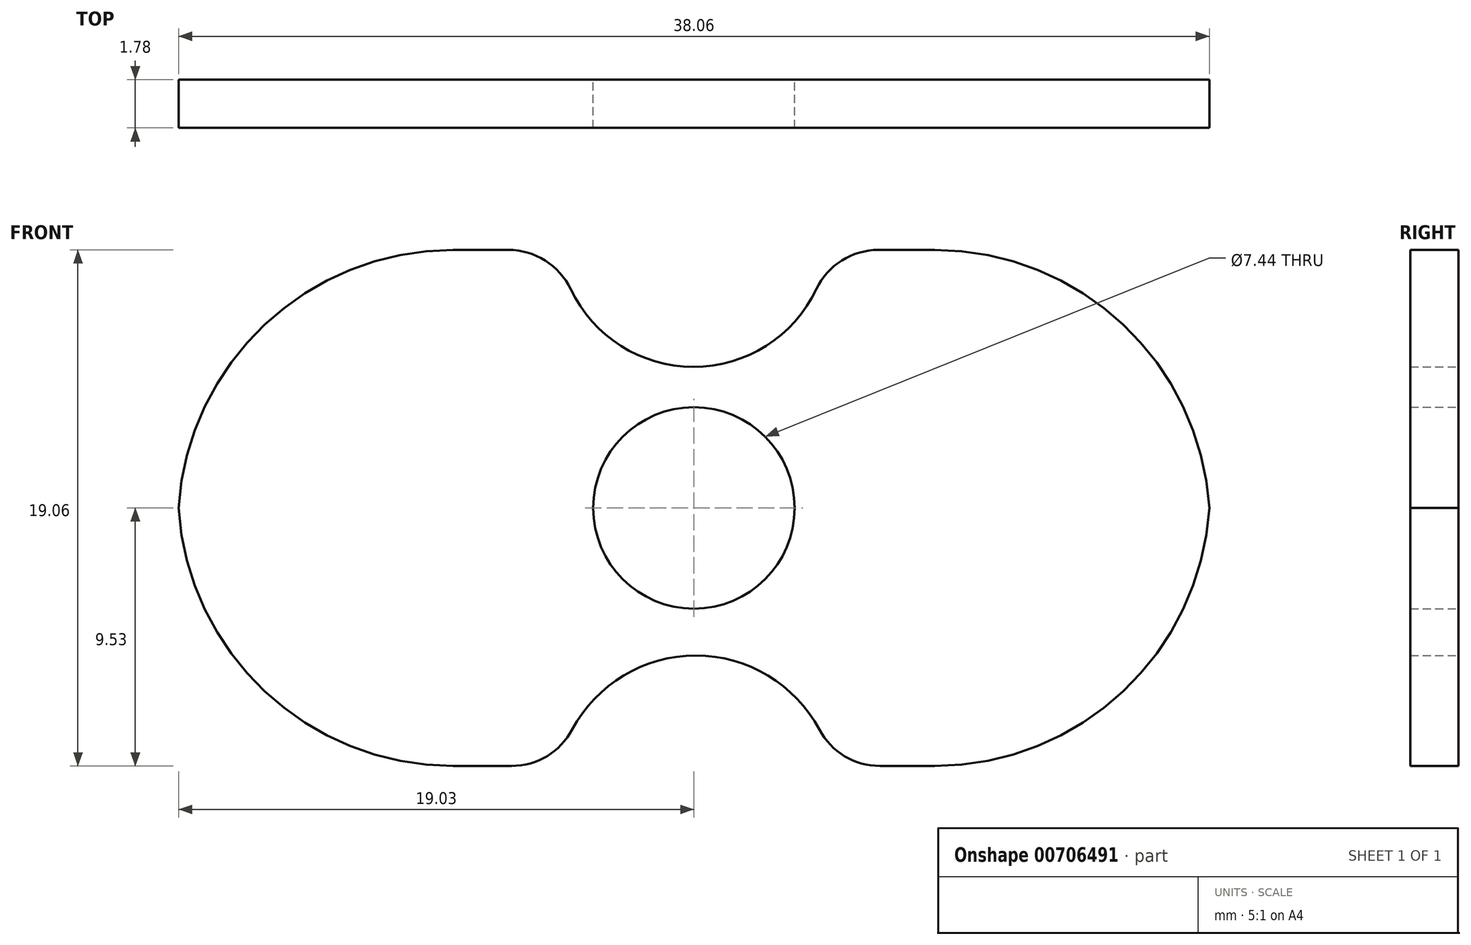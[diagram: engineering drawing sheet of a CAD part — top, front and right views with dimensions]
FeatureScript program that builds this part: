
annotation { "Feature Type Name" : "Feature", "Feature Type Description" : "" }
export const myFeature = defineFeature(function(context is Context, id is Id, definition is map)
    precondition{}
    {
        {
            var Q0;
            Q0=qCreatedBy(makeId("Front.planeOp"),FACE);
            var sketch = newSketch(context, id + "F0", { "sketchPlane" : qUnion([Q0])});
            skLineSegment(sketch, "E0.bottom", {"start": v(19.05, 9.53) * mm, "end": v(-19.05, 9.53) * mm});
            skLineSegment(sketch, "E0.top", {"start": v(19.05, -9.53) * mm, "end": v(-19.05, -9.53) * mm});
            skLineSegment(sketch, "E0.left", {"start": v(19.05, 9.53) * mm, "end": v(19.05, -9.53) * mm});
            skLineSegment(sketch, "E0.right", {"start": v(-19.05, 9.53) * mm, "end": v(-19.05, -9.53) * mm});
            skPoint(sketch, "E0.middle", {"position": v(0, 0) * mm});
            skArc(sketch, "E1", {"start": v(5.13, -9.53) * mm, "mid": v(0.07, -5.45) * mm, "end": v(-4.99, -9.53) * mm});
            skArc(sketch, "E2", {"start": v(-4.99, 9.53) * mm, "mid": v(-0.02, 5.2) * mm, "end": v(4.96, 9.53) * mm});
            skCircle(sketch, "E3", {"center": v(0, 0) * mm, "radius": 3.72 * mm});
            skSolve(sketch);
        }
        {
            var Q0;
            {var subQ0=sQuery(id+"F0.wireOp",EDGE,"E0.left");Q0=makeQuery(id+"F0.imprint","IMPRINT",FACE,{"disambiguationData":[TD([[makeQuery(id+"F0.imprint","IMPRINT",EDGE,{"derivedFrom":subQ0}),-1.0]])]});}
            extrude(context, id + "F1", {"entities" : qUnion([Q0]), "endBound" : BoundingType.SYMMETRIC, "depth" : 1.78 * mm, "offsetDistance" : 25.4 * mm});
        }
        {
            var Q0;
            Q0=makeQuery(id+"F1.opExtrude","SWEPT_EDGE",EDGE,{"disambiguationData":[OSD([sQuery(id+"F0.wireOp",EDGE,"E0.bottom"),sQuery(id+"F0.wireOp",EDGE,"E0.right")])]});
            var Q1;
            Q1=makeQuery(id+"F1.opExtrude","SWEPT_EDGE",EDGE,{"disambiguationData":[OSD([sQuery(id+"F0.wireOp",EDGE,"E0.top"),sQuery(id+"F0.wireOp",EDGE,"E0.right")])]});
            var Q2;
            Q2=makeQuery(id+"F1.opExtrude","SWEPT_EDGE",EDGE,{"disambiguationData":[OSD([sQuery(id+"F0.wireOp",EDGE,"E0.bottom"),sQuery(id+"F0.wireOp",EDGE,"E0.left")])]});
            var Q3;
            Q3=makeQuery(id+"F1.opExtrude","SWEPT_EDGE",EDGE,{"disambiguationData":[OSD([sQuery(id+"F0.wireOp",EDGE,"E0.top"),sQuery(id+"F0.wireOp",EDGE,"E0.left")])]});
            fillet(context, id + "F2", {"entities" : qUnion([Q0, Q1, Q2, Q3]), "radius" : 10.16 * mm, "tangentPropagation" : true, "allowEdgeOverflow" : false});
        }
        {
            var Q0;
            {var subQ0=sQuery(id+"F0.wireOp",EDGE,"E2");var subQ1=sQuery(id+"F0.wireOp",EDGE,"E0.bottom");Q0=makeQuery(id+"F1.opExtrude","SWEPT_EDGE",EDGE,{"disambiguationData":[OSD([subQ1,subQ0]),TDD([makeQuery(id+"F0.imprint","INTERSECT",VERTEX,{"disambiguationData":[OD(0.0)],"derivedFrom":[subQ1,subQ0]})])]});}
            var Q1;
            {var subQ0=sQuery(id+"F0.wireOp",EDGE,"E2");var subQ1=sQuery(id+"F0.wireOp",EDGE,"E0.bottom");Q1=makeQuery(id+"F1.opExtrude","SWEPT_EDGE",EDGE,{"disambiguationData":[OSD([subQ1,subQ0]),TDD([makeQuery(id+"F0.imprint","INTERSECT",VERTEX,{"disambiguationData":[OD(1.0)],"derivedFrom":[subQ1,subQ0]})])]});}
            var Q2;
            {var subQ0=sQuery(id+"F0.wireOp",EDGE,"E1");var subQ1=sQuery(id+"F0.wireOp",EDGE,"E0.top");Q2=makeQuery(id+"F1.opExtrude","SWEPT_EDGE",EDGE,{"disambiguationData":[OSD([subQ1,subQ0]),TDD([makeQuery(id+"F0.imprint","INTERSECT",VERTEX,{"disambiguationData":[OD(1.0)],"derivedFrom":[subQ1,subQ0]})])]});}
            var Q3;
            {var subQ0=sQuery(id+"F0.wireOp",EDGE,"E1");var subQ1=sQuery(id+"F0.wireOp",EDGE,"E0.top");Q3=makeQuery(id+"F1.opExtrude","SWEPT_EDGE",EDGE,{"disambiguationData":[OSD([subQ1,subQ0]),TDD([makeQuery(id+"F0.imprint","INTERSECT",VERTEX,{"disambiguationData":[OD(0.0)],"derivedFrom":[subQ1,subQ0]})])]});}
            fillet(context, id + "F3", {"entities" : qUnion([Q0, Q1, Q2, Q3]), "radius" : 2.54 * mm, "tangentPropagation" : true, "allowEdgeOverflow" : false});
        }
    });
